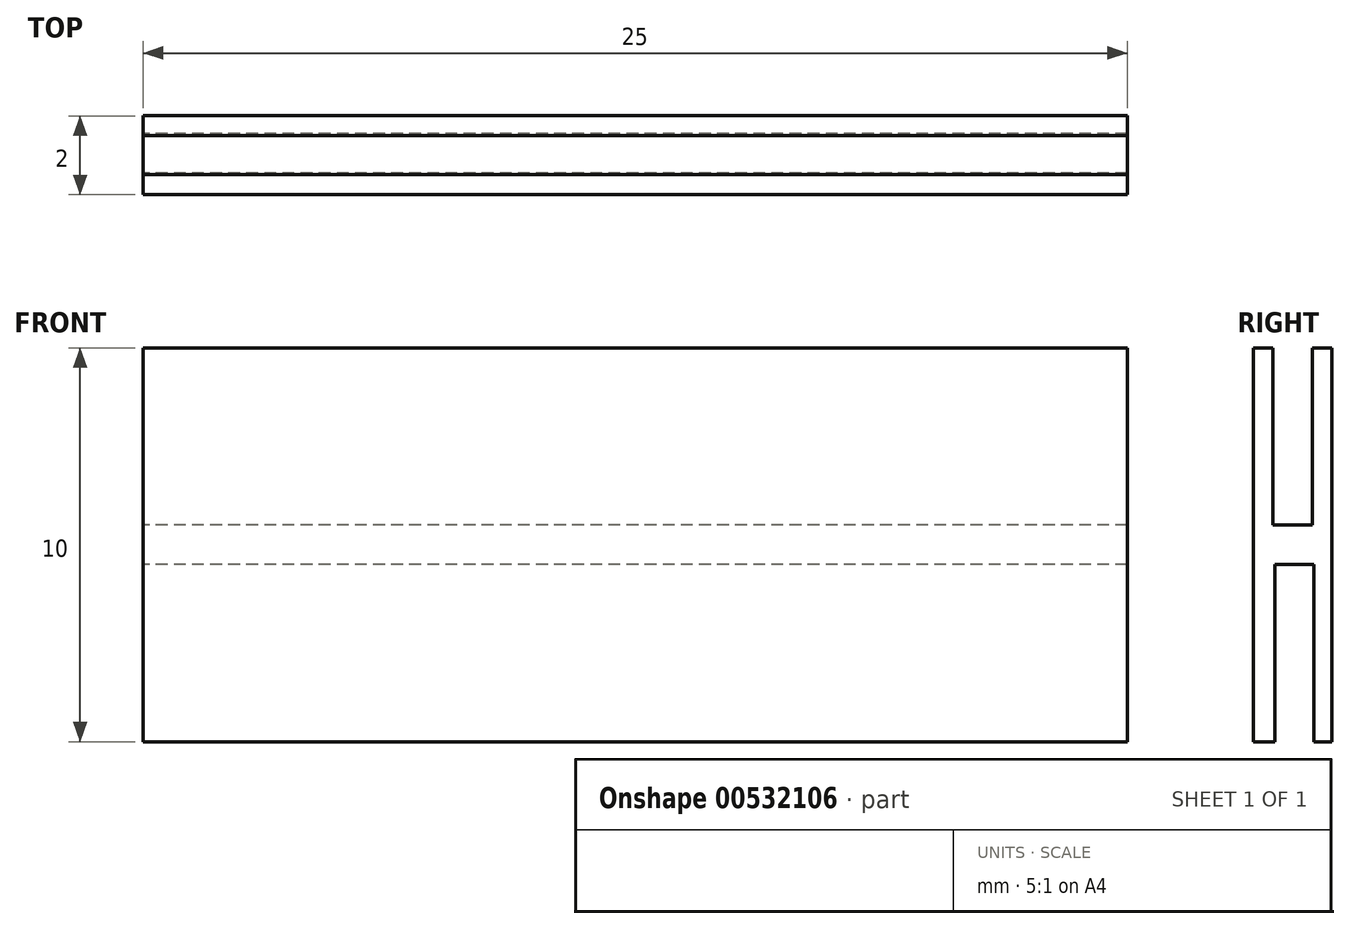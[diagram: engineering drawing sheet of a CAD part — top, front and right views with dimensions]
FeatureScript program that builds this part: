
annotation { "Feature Type Name" : "Feature", "Feature Type Description" : "" }
export const myFeature = defineFeature(function(context is Context, id is Id, definition is map)
    precondition{}
    {
        {
            var Q0;
            Q0=qCreatedBy(makeId("Right.planeOp"),FACE);
            var sketch = newSketch(context, id + "F0", { "sketchPlane" : qUnion([Q0])});
            skLineSegment(sketch, "E0", {"start": v(0.25, -7.77) * mm, "end": v(0.8, -7.77) * mm});
            skLineSegment(sketch, "E1", {"start": v(0.8, -7.77) * mm, "end": v(0.8, -3.27) * mm});
            skLineSegment(sketch, "E2", {"start": v(0.8, -3.27) * mm, "end": v(1.8, -3.27) * mm});
            skLineSegment(sketch, "E3", {"start": v(1.8, -3.27) * mm, "end": v(1.8, -7.77) * mm});
            skLineSegment(sketch, "E4", {"start": v(1.8, -7.77) * mm, "end": v(2.25, -7.77) * mm});
            skLineSegment(sketch, "E5", {"start": v(2.25, -7.77) * mm, "end": v(2.25, 2.23) * mm});
            skLineSegment(sketch, "E6", {"start": v(2.25, 2.23) * mm, "end": v(1.75, 2.23) * mm});
            skLineSegment(sketch, "E7", {"start": v(1.75, 2.23) * mm, "end": v(1.75, -2.27) * mm});
            skLineSegment(sketch, "E8", {"start": v(1.75, -2.27) * mm, "end": v(0.75, -2.27) * mm});
            skLineSegment(sketch, "E9", {"start": v(0.25, -7.77) * mm, "end": v(0.25, 2.23) * mm});
            skLineSegment(sketch, "E10", {"start": v(0.25, 2.23) * mm, "end": v(0.75, 2.23) * mm});
            skLineSegment(sketch, "E11", {"start": v(0.75, 2.23) * mm, "end": v(0.75, -2.27) * mm});
            skSolve(sketch);
        }
        {
            var Q0;
            Q0 = qSketchRegion(id + "F0", true);
            extrude(context, id + "F1", {"entities" : qUnion([Q0]), "depth" : 25 * mm, "offsetDistance" : 25 * mm});
        }
    });
